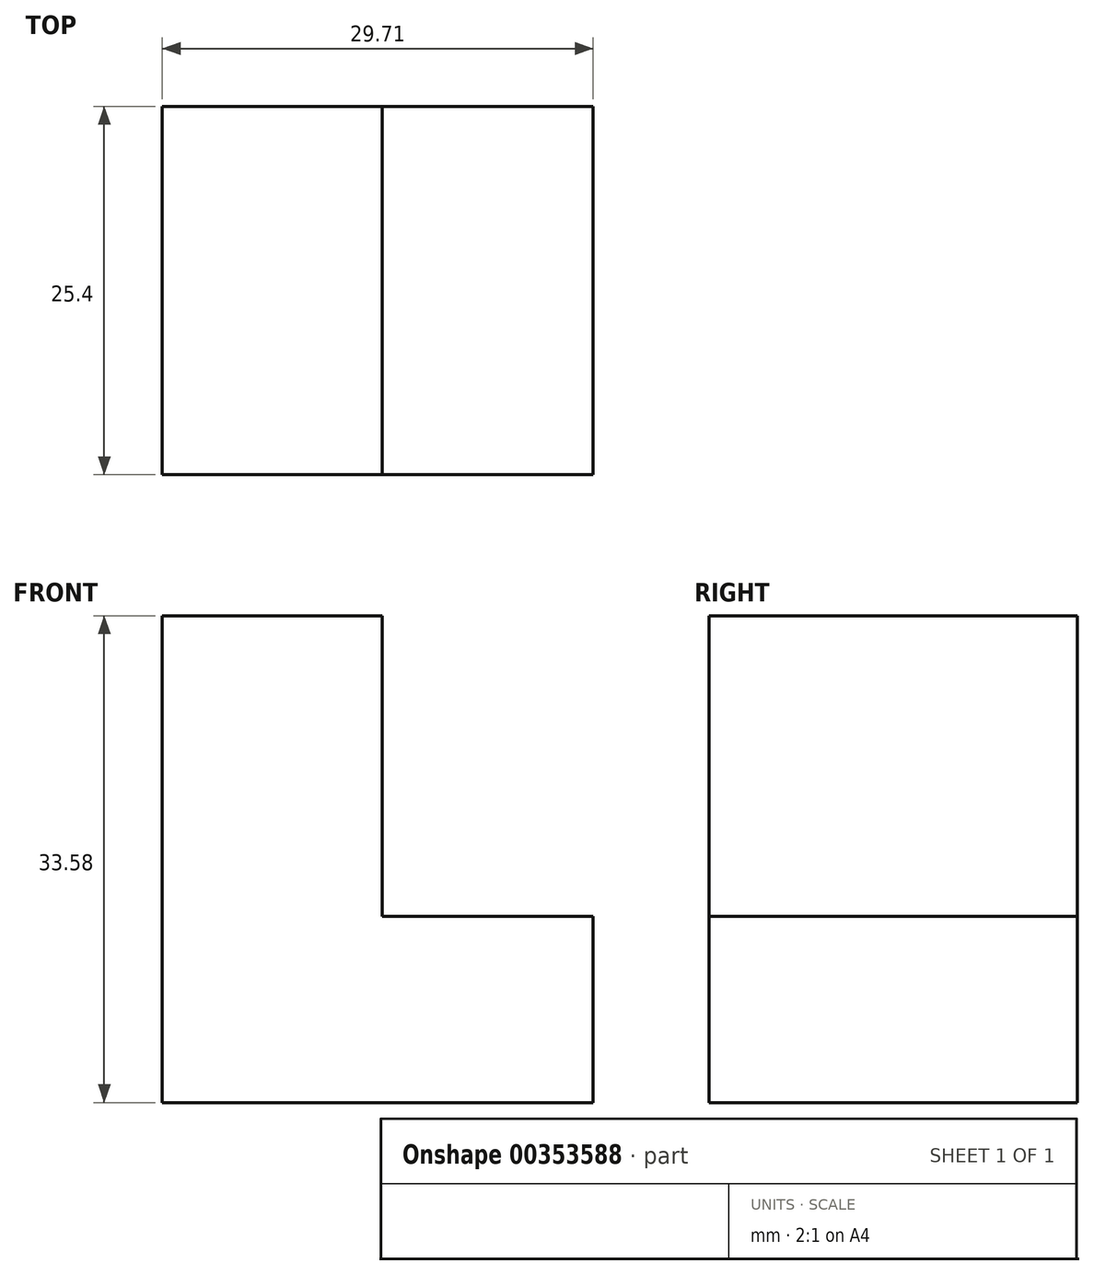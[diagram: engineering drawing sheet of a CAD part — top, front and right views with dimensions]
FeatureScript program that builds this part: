
annotation { "Feature Type Name" : "Feature", "Feature Type Description" : "" }
export const myFeature = defineFeature(function(context is Context, id is Id, definition is map)
    precondition{}
    {
        {
            var Q0;
            Q0=qCreatedBy(makeId("Front.planeOp"),FACE);
            var sketch = newSketch(context, id + "F0", { "sketchPlane" : qUnion([Q0])});
            skLineSegment(sketch, "E0", {"start": v(0, 33.58) * mm, "end": v(15.17, 33.58) * mm});
            skLineSegment(sketch, "E1", {"start": v(15.17, 33.58) * mm, "end": v(15.17, 12.84) * mm});
            skLineSegment(sketch, "E2", {"start": v(15.17, 12.84) * mm, "end": v(29.71, 12.84) * mm});
            skLineSegment(sketch, "E3", {"start": v(29.71, 12.84) * mm, "end": v(29.71, 0) * mm});
            skLineSegment(sketch, "E4", {"start": v(29.71, 0) * mm, "end": v(0, 0) * mm});
            skLineSegment(sketch, "E5", {"start": v(0, 33.58) * mm, "end": v(0, 0) * mm});
            skSolve(sketch);
        }
        {
            var Q0;
            Q0=makeQuery(id+"F0.imprint","IMPRINT",FACE,{"disambiguationData":[TD([[makeQuery(id+"F0.imprint","IMPRINT",EDGE,{"derivedFrom":sQuery(id+"F0.wireOp",EDGE,"E0")}),-1.0]])]});
            extrude(context, id + "F1", {"entities" : qUnion([Q0]), "depth" : 25.4 * mm});
        }
    });
